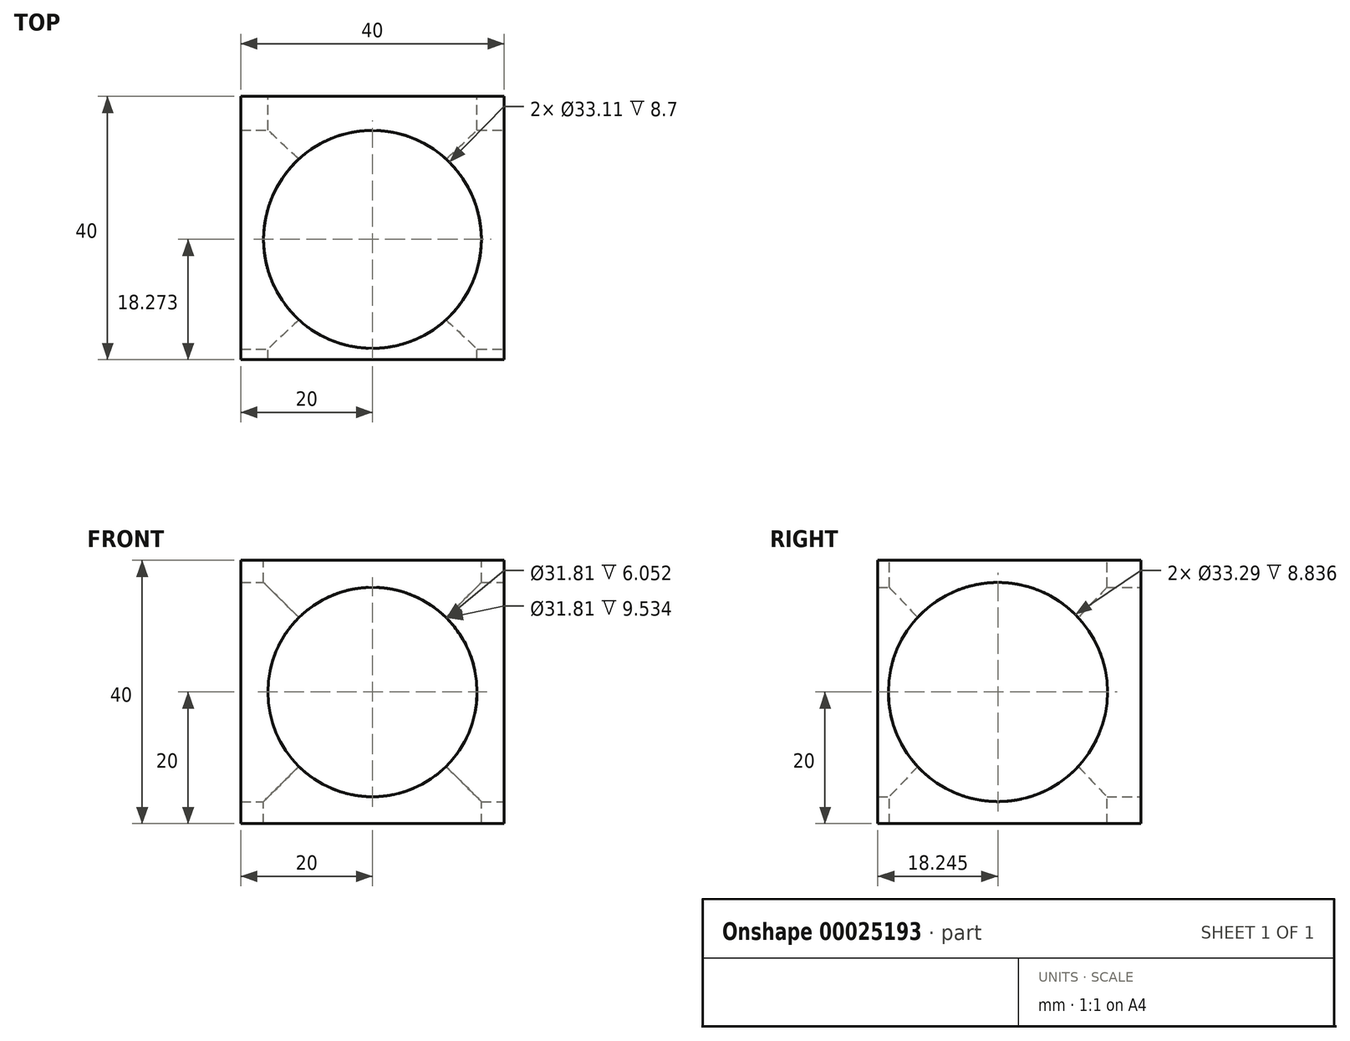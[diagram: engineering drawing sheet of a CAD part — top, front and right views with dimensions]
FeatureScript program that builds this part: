
annotation { "Feature Type Name" : "Feature", "Feature Type Description" : "" }
export const myFeature = defineFeature(function(context is Context, id is Id, definition is map)
    precondition{}
    {
        {
            var Q0;
            Q0=qCreatedBy(makeId("Front.planeOp"),FACE);
            var sketch = newSketch(context, id + "F0", { "sketchPlane" : qUnion([Q0])});
            skLineSegment(sketch, "E0.rect.bottom", {"start": v(-20, 20) * mm, "end": v(20, 20) * mm});
            skLineSegment(sketch, "E0.rect.top", {"start": v(-20, -20) * mm, "end": v(20, -20) * mm});
            skLineSegment(sketch, "E0.rect.left", {"start": v(-20, 20) * mm, "end": v(-20, -20) * mm});
            skLineSegment(sketch, "E0.rect.right", {"start": v(20, 20) * mm, "end": v(20, -20) * mm});
            skPoint(sketch, "E0.rect.middle", {"position": v(0, 0) * mm});
            skSolve(sketch);
        }
        {
            var Q0;
            Q0=makeQuery(id+"F0.imprint","IMPRINT",FACE,{"disambiguationData":[TD([[makeQuery(id+"F0.imprint","IMPRINT",EDGE,{"derivedFrom":sQuery(id+"F0.wireOp",EDGE,"E0.rect.bottom")}),-1.0]])]});
            extrude(context, id + "F1", {"entities" : qUnion([Q0]), "depth" : 40 * mm});
        }
        {
            var Q0;
            Q0=makeQuery(id+"F1.opExtrude","CAP_FACE",FACE,{"disambiguationData":[OSD([sQuery(id+"F0.wireOp",EDGE,"E0.rect.bottom"),sQuery(id+"F0.wireOp",EDGE,"E0.rect.top"),sQuery(id+"F0.wireOp",EDGE,"E0.rect.left"),sQuery(id+"F0.wireOp",EDGE,"E0.rect.right")])],"isStart":true});
            var sketch = newSketch(context, id + "F2", { "sketchPlane" : qUnion([Q0])});
            skCircle(sketch, "E1", {"center": v(0, 0) * mm, "radius": 15.9 * mm});
            skSolve(sketch);
        }
        {
            var Q0;
            Q0=makeQuery(id+"F2.imprint","IMPRINT",FACE,{"disambiguationData":[TD([[makeQuery(id+"F2.imprint","IMPRINT",EDGE,{"derivedFrom":sQuery(id+"F2.wireOp",EDGE,"E1")}),1.0]])]});
            extrude(context, id + "F3", {"entities" : qUnion([Q0]), "operationType" : NewBodyOperationType.REMOVE, "oppositeDirection" : true, "depth" : 40 * mm});
        }
        {
            var Q0;
            Q0=makeQuery(id+"F1.opExtrude","SWEPT_FACE",FACE,{"disambiguationData":[OSD([sQuery(id+"F0.wireOp",EDGE,"E0.rect.bottom")])]});
            var sketch = newSketch(context, id + "F4", { "sketchPlane" : qUnion([Q0])});
            skCircle(sketch, "E2", {"center": v(0, -21.73) * mm, "radius": 16.55 * mm});
            skSolve(sketch);
        }
        {
            var Q0;
            Q0=makeQuery(id+"F4.imprint","IMPRINT",FACE,{"disambiguationData":[TD([[makeQuery(id+"F4.imprint","IMPRINT",EDGE,{"derivedFrom":sQuery(id+"F4.wireOp",EDGE,"E2")}),1.0]])]});
            extrude(context, id + "F5", {"entities" : qUnion([Q0]), "operationType" : NewBodyOperationType.REMOVE, "oppositeDirection" : true, "depth" : 40 * mm});
        }
        {
            var Q0;
            Q0=makeQuery(id+"F1.opExtrude","SWEPT_FACE",FACE,{"disambiguationData":[OSD([sQuery(id+"F0.wireOp",EDGE,"E0.rect.right")])]});
            var sketch = newSketch(context, id + "F6", { "sketchPlane" : qUnion([Q0])});
            skCircle(sketch, "E3", {"center": v(-21.75, 0) * mm, "radius": 16.64 * mm});
            skSolve(sketch);
        }
        {
            var Q0;
            Q0=makeQuery(id+"F6.imprint","IMPRINT",FACE,{"disambiguationData":[TD([[makeQuery(id+"F6.imprint","IMPRINT",EDGE,{"derivedFrom":sQuery(id+"F6.wireOp",EDGE,"E3")}),1.0]])]});
            extrude(context, id + "F7", {"entities" : qUnion([Q0]), "operationType" : NewBodyOperationType.REMOVE, "oppositeDirection" : true, "depth" : 40 * mm});
        }
    });
